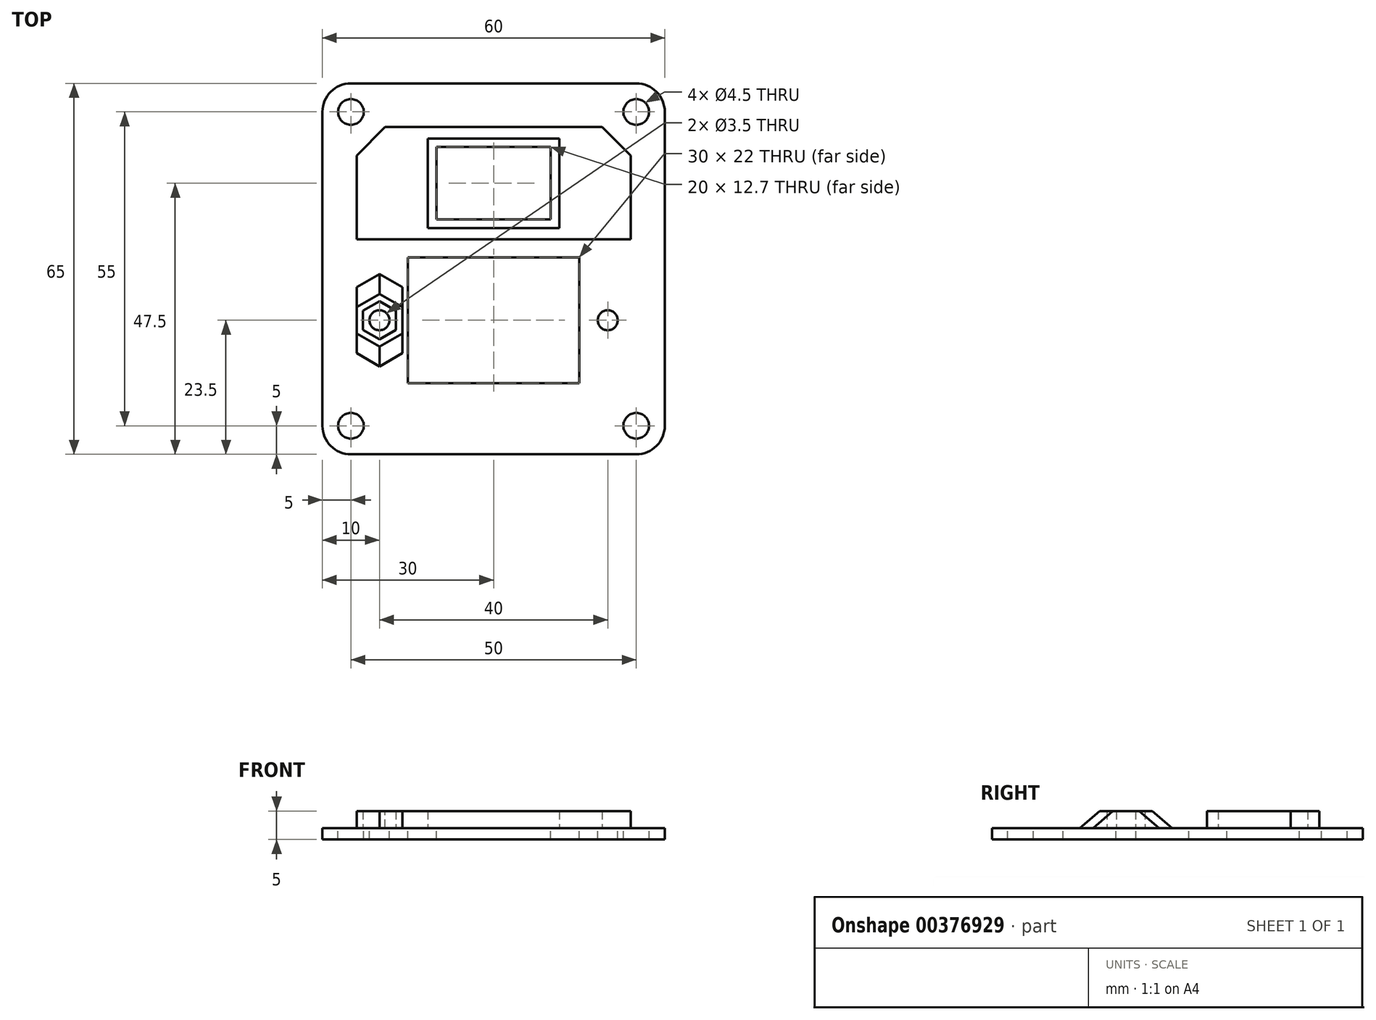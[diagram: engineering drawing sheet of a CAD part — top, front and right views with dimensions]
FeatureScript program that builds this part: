
annotation { "Feature Type Name" : "Feature", "Feature Type Description" : "" }
export const myFeature = defineFeature(function(context is Context, id is Id, definition is map)
    precondition{}
    {
        {
            var Q0;
            Q0=qCreatedBy(makeId("Top.planeOp"),FACE);
            var sketch = newSketch(context, id + "F0", { "sketchPlane" : qUnion([Q0])});
            skLineSegment(sketch, "E0.bottom", {"start": v(-30, -32.5) * mm, "end": v(30, -32.5) * mm});
            skLineSegment(sketch, "E0.top", {"start": v(-30, 32.5) * mm, "end": v(30, 32.5) * mm});
            skLineSegment(sketch, "E0.left", {"start": v(-30, -32.5) * mm, "end": v(-30, 32.5) * mm});
            skLineSegment(sketch, "E0.right", {"start": v(30, -32.5) * mm, "end": v(30, 32.5) * mm});
            skPoint(sketch, "E1", {"position": v(0, -32.5) * mm});
            skPoint(sketch, "E2", {"position": v(-30, 0) * mm});
            skSolve(sketch);
        }
        {
            var Q0;
            Q0=makeQuery(id+"F0.imprint","IMPRINT",FACE,{"disambiguationData":[TD([[makeQuery(id+"F0.imprint","IMPRINT",EDGE,{"derivedFrom":sQuery(id+"F0.wireOp",EDGE,"E0.bottom")}),1.0]])]});
            extrude(context, id + "F1", {"entities" : qUnion([Q0]), "depth" : 2 * mm});
        }
        {
            var Q0;
            Q0=makeQuery(id+"F1.opExtrude","CAP_FACE",FACE,{"disambiguationData":[OSD([sQuery(id+"F0.wireOp",EDGE,"E0.bottom"),sQuery(id+"F0.wireOp",EDGE,"E0.top"),sQuery(id+"F0.wireOp",EDGE,"E0.left"),sQuery(id+"F0.wireOp",EDGE,"E0.right")])],"isStart":false});
            var sketch = newSketch(context, id + "F2", { "sketchPlane" : qUnion([Q0])});
            skLineSegment(sketch, "E3.bottom", {"start": v(-10, 21.35) * mm, "end": v(10, 21.35) * mm});
            skLineSegment(sketch, "E3.top", {"start": v(-10, 8.65) * mm, "end": v(10, 8.65) * mm});
            skLineSegment(sketch, "E3.left", {"start": v(-10, 21.35) * mm, "end": v(-10, 8.65) * mm});
            skLineSegment(sketch, "E3.right", {"start": v(10, 21.35) * mm, "end": v(10, 8.65) * mm});
            skPoint(sketch, "E4", {"position": v(0, 8.65) * mm});
            skPoint(sketch, "E5", {"position": v(-10, 15) * mm});
            skSolve(sketch);
        }
        {
            var Q0;
            Q0=makeQuery(id+"F2.imprint","IMPRINT",FACE,{"disambiguationData":[TD([[makeQuery(id+"F2.imprint","IMPRINT",EDGE,{"derivedFrom":sQuery(id+"F2.wireOp",EDGE,"E3.bottom")}),-1.0]])]});
            extrude(context, id + "F3", {"entities" : qUnion([Q0]), "operationType" : NewBodyOperationType.REMOVE, "oppositeDirection" : true, "depth" : 25 * mm});
        }
        {
            var Q0;
            Q0=makeQuery(id+"F1.opExtrude","CAP_FACE",FACE,{"disambiguationData":[OSD([sQuery(id+"F0.wireOp",EDGE,"E0.bottom"),sQuery(id+"F0.wireOp",EDGE,"E0.top"),sQuery(id+"F0.wireOp",EDGE,"E0.left"),sQuery(id+"F0.wireOp",EDGE,"E0.right")])],"isStart":false});
            var sketch = newSketch(context, id + "F4", { "sketchPlane" : qUnion([Q0])});
            skLineSegment(sketch, "E6.bottom", {"start": v(-15, -20) * mm, "end": v(15, -20) * mm});
            skLineSegment(sketch, "E6.top", {"start": v(-15, 2) * mm, "end": v(15, 2) * mm});
            skLineSegment(sketch, "E6.left", {"start": v(-15, -20) * mm, "end": v(-15, 2) * mm});
            skLineSegment(sketch, "E6.right", {"start": v(15, -20) * mm, "end": v(15, 2) * mm});
            skPoint(sketch, "E7", {"position": v(0, -20) * mm});
            skCircle(sketch, "E8", {"center": v(-20, -9) * mm, "radius": 1.75 * mm});
            skCircle(sketch, "E9", {"center": v(20, -9) * mm, "radius": 1.75 * mm});
            skLineSegment(sketch, "E10", {"start": v(-20, -9) * mm, "end": v(20, -9) * mm, "construction": true});
            skPoint(sketch, "E11", {"position": v(0, -9) * mm});
            skPoint(sketch, "E12", {"position": v(15, -9) * mm});
            skSolve(sketch);
        }
        {
            var Q0;
            Q0=makeQuery(id+"F4.imprint","IMPRINT",FACE,{"disambiguationData":[TD([[makeQuery(id+"F4.imprint","IMPRINT",EDGE,{"derivedFrom":sQuery(id+"F4.wireOp",EDGE,"E8")}),1.0]])]});
            var Q1;
            Q1=makeQuery(id+"F4.imprint","IMPRINT",FACE,{"disambiguationData":[TD([[makeQuery(id+"F4.imprint","IMPRINT",EDGE,{"derivedFrom":sQuery(id+"F4.wireOp",EDGE,"E6.bottom")}),1.0]])]});
            var Q2;
            Q2=makeQuery(id+"F4.imprint","IMPRINT",FACE,{"disambiguationData":[TD([[makeQuery(id+"F4.imprint","IMPRINT",EDGE,{"derivedFrom":sQuery(id+"F4.wireOp",EDGE,"E9")}),1.0]])]});
            extrude(context, id + "F5", {"entities" : qUnion([Q0, Q1, Q2]), "operationType" : NewBodyOperationType.REMOVE, "oppositeDirection" : true, "depth" : 25 * mm});
        }
        {
            var Q0;
            Q0=makeQuery(id+"F1.opExtrude","CAP_FACE",FACE,{"disambiguationData":[OSD([sQuery(id+"F0.wireOp",EDGE,"E0.bottom"),sQuery(id+"F0.wireOp",EDGE,"E0.top"),sQuery(id+"F0.wireOp",EDGE,"E0.left"),sQuery(id+"F0.wireOp",EDGE,"E0.right")])],"isStart":false});
            var sketch = newSketch(context, id + "F6", { "sketchPlane" : qUnion([Q0])});
            skCircle(sketch, "E13.0", {"center": v(-20, -9) * mm, "radius": 1.75 * mm});
            skCircle(sketch, "E14.0", {"center": v(20, -9) * mm, "radius": 1.75 * mm});
            skCircle(sketch, "E15.cCircle", {"center": v(-20, -9) * mm, "radius": 2.9 * mm, "construction": true});
            skLineSegment(sketch, "E15.0", {"start": v(-22.9, -10.67) * mm, "end": v(-22.9, -7.33) * mm});
            skLineSegment(sketch, "E15.1", {"start": v(-22.9, -7.33) * mm, "end": v(-20, -5.65) * mm});
            skLineSegment(sketch, "E15.2", {"start": v(-20, -5.65) * mm, "end": v(-17.1, -7.33) * mm});
            skLineSegment(sketch, "E15.3", {"start": v(-17.1, -7.33) * mm, "end": v(-17.1, -10.67) * mm});
            skLineSegment(sketch, "E15.4", {"start": v(-17.1, -10.67) * mm, "end": v(-20, -12.35) * mm});
            skLineSegment(sketch, "E15.5", {"start": v(-20, -12.35) * mm, "end": v(-22.9, -10.67) * mm});
            skPoint(sketch, "E15.0.midPoint", {"position": v(-22.9, -9) * mm});
            skCircle(sketch, "E16.cCircle", {"center": v(-20, -9) * mm, "radius": 4 * mm, "construction": true});
            skLineSegment(sketch, "E16.0", {"start": v(-24, -11.3) * mm, "end": v(-24, -6.7) * mm});
            skLineSegment(sketch, "E16.1", {"start": v(-24, -6.7) * mm, "end": v(-20, -4.38) * mm});
            skLineSegment(sketch, "E16.2", {"start": v(-20, -4.38) * mm, "end": v(-16, -6.7) * mm});
            skLineSegment(sketch, "E16.3", {"start": v(-16, -6.7) * mm, "end": v(-16, -11.3) * mm});
            skLineSegment(sketch, "E16.4", {"start": v(-16, -11.3) * mm, "end": v(-20, -13.62) * mm});
            skLineSegment(sketch, "E16.5", {"start": v(-20, -13.62) * mm, "end": v(-24, -11.3) * mm});
            skPoint(sketch, "E16.0.midPoint", {"position": v(-24, -9) * mm});
            skSolve(sketch);
        }
        {
            var Q0;
            Q0=makeQuery(id+"F6.imprint","IMPRINT",FACE,{"disambiguationData":[TD([[makeQuery(id+"F6.imprint","IMPRINT",EDGE,{"derivedFrom":sQuery(id+"F6.wireOp",EDGE,"E15.0")}),1.0]])]});
            extrude(context, id + "F7", {"entities" : qUnion([Q0]), "operationType" : NewBodyOperationType.ADD, "depth" : 3 * mm});
        }
        {
            var Q0;
            Q0=makeQuery(id+"F7.opExtrude","CAP_EDGE",EDGE,{"disambiguationData":[OSD([sQuery(id+"F6.wireOp",EDGE,"E16.5")])],"isStart":true});
            var Q1;
            Q1=makeQuery(id+"F7.opExtrude","CAP_EDGE",EDGE,{"disambiguationData":[OSD([sQuery(id+"F6.wireOp",EDGE,"E16.4")])],"isStart":true});
            var Q2;
            Q2=makeQuery(id+"F7.opExtrude","CAP_EDGE",EDGE,{"disambiguationData":[OSD([sQuery(id+"F6.wireOp",EDGE,"E16.1")])],"isStart":true});
            var Q3;
            Q3=makeQuery(id+"F7.opExtrude","CAP_EDGE",EDGE,{"disambiguationData":[OSD([sQuery(id+"F6.wireOp",EDGE,"E16.2")])],"isStart":true});
            chamfer(context, id + "F8", {"entities" : qUnion([Q0, Q1, Q2, Q3]), "width" : 3 * mm, "tangentPropagation" : true});
        }
        {
            var Q0;
            {var subQ5=sQuery(id+"F0.wireOp",EDGE,"E0.left");var subQ10=sQuery(id+"F0.wireOp",EDGE,"E0.right");var subQ13=sQuery(id+"F0.wireOp",EDGE,"E0.bottom");var subQ14=makeQuery(id+"F1.opExtrude","SWEPT_FACE",FACE,{"disambiguationData":[OSD([subQ13])]});var subQ21=sQuery(id+"F0.wireOp",EDGE,"E0.top");Q0=makeQuery(id+"F2Lr6yohGFZljGb_1.1.F7.boolean.opBoolean","SPLIT",FACE,{"disambiguationData":[TD([subQ14])],"derivedFrom":makeQuery(id+"F7.boolean.opBoolean","SPLIT",FACE,{"disambiguationData":[TD([subQ14])],"derivedFrom":makeQuery(id+"F1.opExtrude","CAP_FACE",FACE,{"disambiguationData":[OSD([subQ13,subQ21,subQ5,subQ10])],"isStart":false})})});}
            var sketch = newSketch(context, id + "F9", { "sketchPlane" : qUnion([Q0])});
            skLineSegment(sketch, "E17.bottom", {"start": v(-25, 27.5) * mm, "end": v(25, 27.5) * mm, "construction": true});
            skLineSegment(sketch, "E17.top", {"start": v(-25, -27.5) * mm, "end": v(25, -27.5) * mm, "construction": true});
            skLineSegment(sketch, "E17.left", {"start": v(-25, 27.5) * mm, "end": v(-25, -27.5) * mm, "construction": true});
            skLineSegment(sketch, "E17.right", {"start": v(25, 27.5) * mm, "end": v(25, -27.5) * mm, "construction": true});
            skPoint(sketch, "E18", {"position": v(-25, 0) * mm});
            skPoint(sketch, "E19", {"position": v(0, 27.5) * mm});
            skPoint(sketch, "E20", {"position": v(-25, 27.5) * mm});
            skPoint(sketch, "E21", {"position": v(25, 27.5) * mm});
            skPoint(sketch, "E22", {"position": v(25, -27.5) * mm});
            skPoint(sketch, "E23", {"position": v(-25, -27.5) * mm});
            skSolve(sketch);
        }
        {
            var Q0;
            Q0=sQuery(id+"F9.wireOp",VERTEX,"E20");
            var Q1;
            Q1=sQuery(id+"F9.wireOp",VERTEX,"E21");
            var Q2;
            Q2=sQuery(id+"F9.wireOp",VERTEX,"E22");
            var Q3;
            Q3=sQuery(id+"F9.wireOp",VERTEX,"E23");
            var Q4;
            Q4=makeQuery(id+"F1.opExtrude","SWEPT_BODY",BODY,{"disambiguationData":[OSD([sQuery(id+"F0.wireOp",EDGE,"E0.bottom"),sQuery(id+"F0.wireOp",EDGE,"E0.top"),sQuery(id+"F0.wireOp",EDGE,"E0.left"),sQuery(id+"F0.wireOp",EDGE,"E0.right")])]});
            hole(context, id + "F10", {"style" : HoleStyle.SIMPLE, "endStyle" : HoleEndStyle.THROUGH, "holeDiameter" : 4.5 * mm, "isTappedThrough" : true, "tappedDepth" : 12 * mm, "tapClearance" : 3, "locations" : qUnion([Q0, Q1, Q2, Q3]), "scope" : qUnion([Q4])});
        }
        {
            var Q0;
            Q0=makeQuery(id+"F1.opExtrude","SWEPT_EDGE",EDGE,{"disambiguationData":[OSD([sQuery(id+"F0.wireOp",EDGE,"E0.top"),sQuery(id+"F0.wireOp",EDGE,"E0.right")])]});
            var Q1;
            Q1=makeQuery(id+"F1.opExtrude","SWEPT_EDGE",EDGE,{"disambiguationData":[OSD([sQuery(id+"F0.wireOp",EDGE,"E0.top"),sQuery(id+"F0.wireOp",EDGE,"E0.left")])]});
            var Q2;
            Q2=makeQuery(id+"F1.opExtrude","SWEPT_EDGE",EDGE,{"disambiguationData":[OSD([sQuery(id+"F0.wireOp",EDGE,"E0.bottom"),sQuery(id+"F0.wireOp",EDGE,"E0.right")])]});
            var Q3;
            Q3=makeQuery(id+"F1.opExtrude","SWEPT_EDGE",EDGE,{"disambiguationData":[OSD([sQuery(id+"F0.wireOp",EDGE,"E0.bottom"),sQuery(id+"F0.wireOp",EDGE,"E0.left")])]});
            fillet(context, id + "F11", {"entities" : qUnion([Q0, Q1, Q2, Q3]), "radius" : 5 * mm, "tangentPropagation" : true, "allowEdgeOverflow" : false});
        }
        {
            var Q0;
            {var subQ5=sQuery(id+"F0.wireOp",EDGE,"E0.left");var subQ10=sQuery(id+"F0.wireOp",EDGE,"E0.right");var subQ13=sQuery(id+"F0.wireOp",EDGE,"E0.bottom");var subQ14=makeQuery(id+"F1.opExtrude","SWEPT_FACE",FACE,{"disambiguationData":[OSD([subQ13])]});var subQ21=sQuery(id+"F0.wireOp",EDGE,"E0.top");Q0=makeQuery(id+"F2Lr6yohGFZljGb_1.1.F7.boolean.opBoolean","SPLIT",FACE,{"disambiguationData":[TD([subQ14])],"derivedFrom":makeQuery(id+"F7.boolean.opBoolean","SPLIT",FACE,{"disambiguationData":[TD([subQ14])],"derivedFrom":makeQuery(id+"F1.opExtrude","CAP_FACE",FACE,{"disambiguationData":[OSD([subQ13,subQ21,subQ5,subQ10])],"isStart":false})})});}
            var sketch = newSketch(context, id + "F12", { "sketchPlane" : qUnion([Q0])});
            skLineSegment(sketch, "E24.bottom", {"start": v(-11.5, 7.15) * mm, "end": v(11.5, 7.15) * mm});
            skLineSegment(sketch, "E24.left", {"start": v(-11.5, 7.15) * mm, "end": v(-11.5, 22.85) * mm});
            skLineSegment(sketch, "E24.right", {"start": v(11.5, 7.15) * mm, "end": v(11.5, 22.85) * mm});
            skLineSegment(sketch, "E25.bottom", {"start": v(-24, 5.15) * mm, "end": v(24, 5.15) * mm});
            skLineSegment(sketch, "E25.top", {"start": v(-24, 24.85) * mm, "end": v(24, 24.85) * mm});
            skLineSegment(sketch, "E25.left", {"start": v(-24, 5.15) * mm, "end": v(-24, 24.85) * mm});
            skLineSegment(sketch, "E25.right", {"start": v(24, 5.15) * mm, "end": v(24, 24.85) * mm});
            skPoint(sketch, "E26", {"position": v(0, 7.15) * mm});
            skPoint(sketch, "E27", {"position": v(-24, 15) * mm});
            skPoint(sketch, "E28", {"position": v(-11.5, 15) * mm});
            skLineSegment(sketch, "E29", {"start": v(-11.5, 22.85) * mm, "end": v(11.5, 22.85) * mm});
            skLineSegment(sketch, "E30.0", {"start": v(-10, 21.35) * mm, "end": v(-10, 8.65) * mm});
            skLineSegment(sketch, "E31.0", {"start": v(-10, 21.35) * mm, "end": v(10, 21.35) * mm});
            skPoint(sketch, "E32", {"position": v(-10, 15) * mm});
            skSolve(sketch);
        }
        {
            var Q0;
            Q0=makeQuery(id+"F12.imprint","IMPRINT",FACE,{"disambiguationData":[TD([[makeQuery(id+"F12.imprint","IMPRINT",EDGE,{"derivedFrom":sQuery(id+"F12.wireOp",EDGE,"E24.bottom")}),-1.0]])]});
            extrude(context, id + "F13", {"entities" : qUnion([Q0]), "operationType" : NewBodyOperationType.ADD, "depth" : 3 * mm});
        }
        {
            var Q0;
            Q0=makeQuery(id+"F13.opExtrude","SWEPT_EDGE",EDGE,{"disambiguationData":[OSD([sQuery(id+"F12.wireOp",EDGE,"E25.top"),sQuery(id+"F12.wireOp",EDGE,"E25.right")])]});
            var Q1;
            Q1=makeQuery(id+"F13.opExtrude","SWEPT_EDGE",EDGE,{"disambiguationData":[OSD([sQuery(id+"F12.wireOp",EDGE,"E25.top"),sQuery(id+"F12.wireOp",EDGE,"E25.left")])]});
            chamfer(context, id + "F14", {"entities" : qUnion([Q0, Q1]), "width" : 5 * mm, "tangentPropagation" : true});
        }
    });
